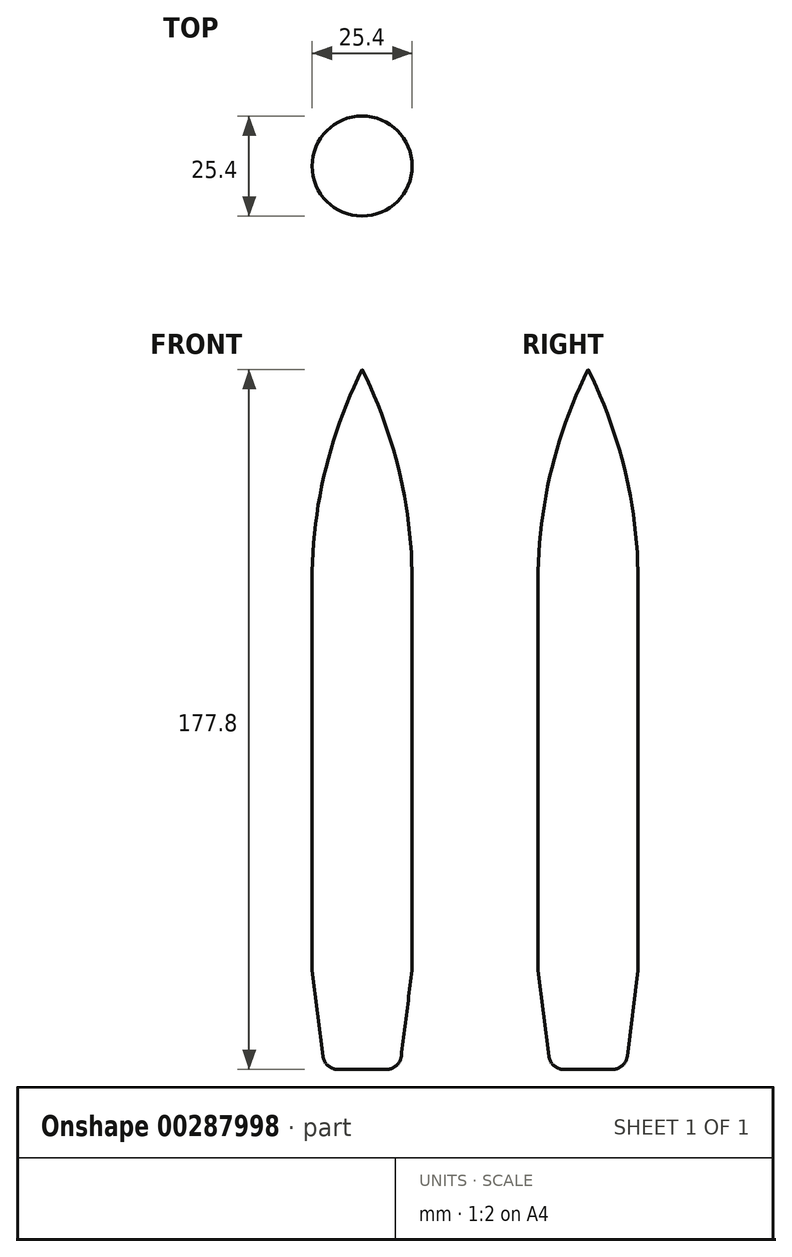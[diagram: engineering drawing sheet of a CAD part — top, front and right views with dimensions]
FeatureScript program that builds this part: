
annotation { "Feature Type Name" : "Feature", "Feature Type Description" : "" }
export const myFeature = defineFeature(function(context is Context, id is Id, definition is map)
    precondition{}
    {
        {
            var Q0;
            Q0=qCreatedBy(makeId("Top.planeOp"),FACE);
            var sketch = newSketch(context, id + "F0", { "sketchPlane" : qUnion([Q0])});
            skCircle(sketch, "E0", {"center": v(0, 0) * mm, "radius": 12.7 * mm});
            skSolve(sketch);
        }
        {
            var Q0;
            Q0 = qSketchRegion(id + "F0", true);
            extrude(context, id + "F1", {"entities" : qUnion([Q0]), "endBound" : BoundingType.SYMMETRIC, "depth" : 127 * mm});
        }
        {
            var Q0;
            Q0=makeQuery(id+"F1.opExtrude","CAP_FACE",FACE,{"disambiguationData":[OSD([sQuery(id+"F0.wireOp",EDGE,"E0")])],"isStart":false});
            var sketch = newSketch(context, id + "F2", { "sketchPlane" : qUnion([Q0])});
            skCircle(sketch, "E1", {"center": v(0, 0) * mm, "radius": 12.7 * mm});
            skSolve(sketch);
        }
        {
            var Q0;
            Q0=makeQuery(id+"F2.imprint","IMPRINT",FACE,{"disambiguationData":[TD([[makeQuery(id+"F2.imprint","IMPRINT",EDGE,{"derivedFrom":sQuery(id+"F2.wireOp",EDGE,"E1")}),1.0]])]});
            cPlane(context, id + "F3", {"entities" : qUnion([Q0]), "cplaneType" : CPlaneType.OFFSET, "offset" : 25.4 * mm, "width" : 152.4 * mm, "height" : 152.4 * mm});
        }
        {
            var Q0;
            Q0=qCreatedBy(id+"F3.planeOp",FACE);
            var sketch = newSketch(context, id + "F4", { "sketchPlane" : qUnion([Q0])});
            skCircle(sketch, "E2", {"center": v(0, 0) * mm, "radius": 1.08 * mm});
            skSolve(sketch);
        }
        {
            var Q1;
            Q1=sQuery(id+"F4.wireOp",VERTEX,"E2.center");
            var Q2;
            Q2=makeQuery(id+"F2.imprint","IMPRINT",FACE,{"disambiguationData":[TD([[makeQuery(id+"F2.imprint","IMPRINT",EDGE,{"derivedFrom":sQuery(id+"F2.wireOp",EDGE,"E1")}),1.0]])]});
            loft(context, id + "F5", {"operationType" : NewBodyOperationType.ADD, "sheetProfilesArray" : [{ "sheetProfileEntities" : qUnion([Q1]) }, { "sheetProfileEntities" : qUnion([Q2]) }]});
        }
        {
            var Q0;
            Q0=makeQuery(id+"F5.opLoft","SWEPT_FACE",FACE,{"disambiguationData":[OSD([sQuery(id+"F2.wireOp",EDGE,"E1"),sQuery(id+"F4.wireOp",VERTEX,"E2.center")])]});
            fillet(context, id + "F6", {"entities" : qUnion([Q0]), "radius" : 120.13 * mm, "tangentPropagation" : true, "allowEdgeOverflow" : false});
        }
        {
            var Q0;
            Q0=makeQuery(id+"F1.opExtrude","CAP_FACE",FACE,{"disambiguationData":[OSD([sQuery(id+"F0.wireOp",EDGE,"E0")])],"isStart":true});
            cPlane(context, id + "F7", {"entities" : qUnion([Q0]), "cplaneType" : CPlaneType.OFFSET, "offset" : 25.4 * mm, "width" : 152.4 * mm, "height" : 152.4 * mm});
        }
        {
            var Q0;
            Q0=qCreatedBy(id+"F7.planeOp",FACE);
            var sketch = newSketch(context, id + "F8", { "sketchPlane" : qUnion([Q0])});
            skCircle(sketch, "E3", {"center": v(0, 0) * mm, "radius": 9.53 * mm});
            skSolve(sketch);
        }
        {
            var Q1;
            Q1=makeQuery(id+"F1.opExtrude","CAP_FACE",FACE,{"disambiguationData":[OSD([sQuery(id+"F0.wireOp",EDGE,"E0")])],"isStart":true});
            var Q2;
            Q2=makeQuery(id+"F8.imprint","IMPRINT",FACE,{"disambiguationData":[TD([[makeQuery(id+"F8.imprint","IMPRINT",EDGE,{"derivedFrom":sQuery(id+"F8.wireOp",EDGE,"E3")}),1.0]])]});
            loft(context, id + "F9", {"operationType" : NewBodyOperationType.ADD, "sheetProfilesArray" : [{ "sheetProfileEntities" : qUnion([Q1]) }, { "sheetProfileEntities" : qUnion([Q2]) }]});
        }
        {
            var Q0;
            Q0=makeQuery(id+"F9.opLoft","SWEPT_FACE",FACE,{"disambiguationData":[OSD([sQuery(id+"F0.wireOp",EDGE,"E0"),sQuery(id+"F8.wireOp",EDGE,"E3")])]});
            fillet(context, id + "F10", {"entities" : qUnion([Q0]), "radius" : 3.8 * mm, "tangentPropagation" : true, "allowEdgeOverflow" : false});
        }
    });
